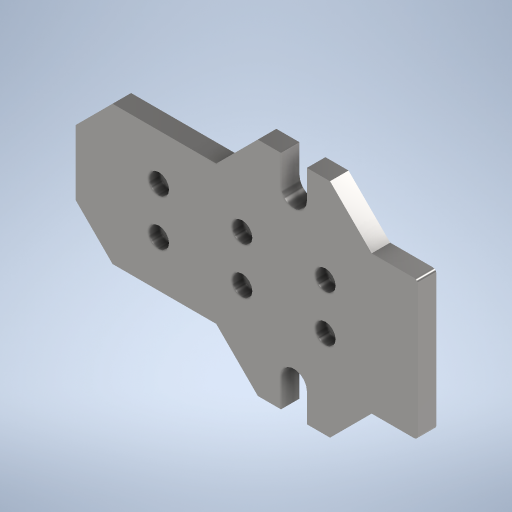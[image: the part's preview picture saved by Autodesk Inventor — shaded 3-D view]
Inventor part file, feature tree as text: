
AUTODESK INVENTOR PART (.ipt)
format: ipt  version: 2023.2 (Build 272271000, 271)  size: 334,848 bytes
history: native  units: mm
features: sketch x2, extrude x1, hole x1
ambient origin geometry x8: Origin, YZ Plane, XZ Plane, XY Plane, X Axis, Y Axis, Z Axis, Center Point
bodies: Solid1 (feature_tree)
feature tree (4):
  extrude  "Extrusion1"  TaperAngle=45.0deg  [1 undecoded]
  hole  "Hole1"  [1 undecoded]
  sketch  "Sketch1"  dims[d13=17.5mm d14=45.0deg]
  sketch  "Sketch2"  dims[d15=17.5mm d16=135.0deg d19=14.0mm d20=15.5mm d21=15.5mm d22=12.5mm d23=45.0deg d24=12.5mm d25=135.0deg d27=14.0mm d28=15.5mm d29=15.5mm d31=12.5mm d32=135.0deg d33=12.5mm d34=135.0deg d35=2.0mm d36=60.0mm d37=185.0mm d38=97.5mm d39=42.5mm d40=4.40571mm d41=92.5mm d42=60.0mm d43=127.58412mm d44=10.0mm d45=0.0mm d46=6.0mm d47=15.0mm d48=11.0mm d49=6.0mm d50=14.3117mm d51=2.0mm d52=20.594885mm d53=50.0mm d54=25.0mm d55=50.0mm d56=45.0mm d57=45.0mm d58=45.0mm d59=45.0mm d60=12.5mm d61=12.5mm d62=12.5mm d63=25.0mm d64=25.0mm]
note: 2 required parameter values undecoded (feature->parameter linkage not recoverable at this tier; creation-order binding heuristic only, values carry confidence <= 0.55)
